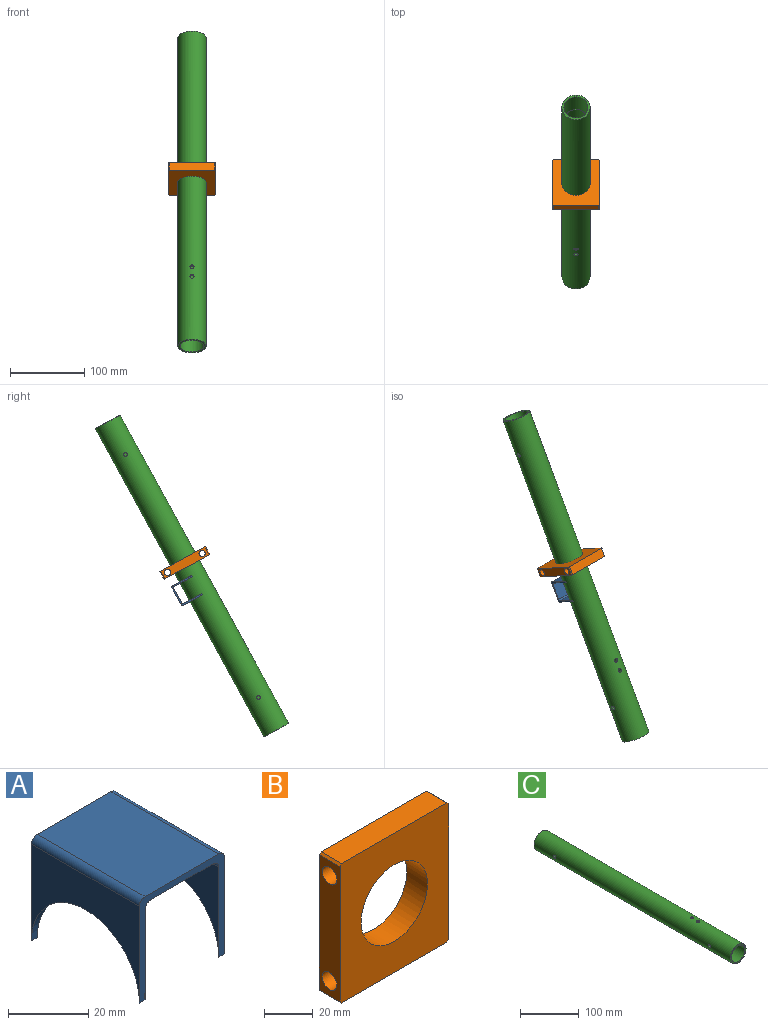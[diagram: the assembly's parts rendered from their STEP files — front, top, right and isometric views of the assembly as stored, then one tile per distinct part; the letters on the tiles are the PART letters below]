
ASSEMBLY  parts=3 mates=2
PART A: 14 faces, bbox 30x38x31.5 mm
  f0: plane 38x29.5mm, normal (1,0,0), area 553.9mm2, adj f6,f7,f9,f10
  f1: plane 38x26mm, normal (0,0,1), area 988mm2, adj f6,f7,f10,f11
  f2: plane 38x29.5mm, normal (-1,0,0), area 553.9mm2, adj f6,f7,f8,f11
  f3: plane 38x27.5mm, normal (1,0,0), area 477.9mm2, adj f6,f7,f8,f12
  f4: plane 38x22mm, normal (0,0,-1), area 836mm2, adj f6,f7,f12,f13
  f5: plane 38x27.5mm, normal (-1,0,0), area 477.9mm2, adj f6,f7,f9,f13
  f6: plane 31.5x30mm, normal (0,-1,0), area 178mm2, adj f0,f1,f2,f3,f4,f5,f8,f9
  f7: plane 31.5x30mm, normal (0,1,0), area 178mm2, adj f0,f1,f2,f3,f4,f5,f8,f9
  f8: cylinder r=19mm len=38mm, axis (-1,0,0), area 119.4mm2, adj f2,f3,f6,f7
  f9: cylinder r=19mm len=38mm, axis (-1,0,0), area 119.4mm2, adj f0,f5,f6,f7
  f10: cylinder r=2mm len=38mm, axis (0,1,0), area 119.4mm2, adj f0,f1,f6,f7
  f11: cylinder r=2mm len=38mm, axis (0,1,0), area 119.4mm2, adj f1,f2,f6,f7
  f12: cylinder r=2mm len=38mm, axis (0,-1,0), area 119.4mm2, adj f3,f4,f6,f7
  f13: cylinder r=2mm len=38mm, axis (0,-1,0), area 119.4mm2, adj f4,f5,f6,f7
PART B: 13 faces, bbox 63x12x70 mm
  f0: plane 61x12mm, normal (0,0,1), area 732mm2, adj f4,f5,f9,f12
  f1: plane 68x12mm, normal (-1,0,0), area 702.5mm2, adj f4,f5,f7,f8,f9,f10
  f2: plane 61x12mm, normal (0,0,-1), area 732mm2, adj f4,f5,f10,f11
  f3: plane 68x12mm, normal (1,0,0), area 702.5mm2, adj f4,f5,f7,f8,f11,f12
  f4: plane 70x63mm, normal (0,-1,0), area 3243.8mm2, adj f0,f1,f2,f3,f6,f9,f10,f11
  f5: plane 70x63mm, normal (0,1,0), area 3243.8mm2, adj f0,f1,f2,f3,f6,f9,f10,f11
  f6: cylinder r=19.25mm len=38.5mm, axis (0,-1,0), area 1451.4mm2, adj f4,f5
  f7: cylinder r=4.25mm len=63mm, axis (-1,0,0), area 1682.3mm2, adj f1,f3
  f8: cylinder r=4.25mm len=63mm, axis (-1,0,0), area 1682.3mm2, adj f1,f3
  f9: plane 12x1mm, normal (-0.71,0,0.71), area 17mm2, adj f0,f1,f4,f5
  f10: plane 12x1mm, normal (-0.71,0,-0.71), area 17mm2, adj f1,f2,f4,f5
  f11: plane 12x1mm, normal (0.71,0,-0.71), area 17mm2, adj f2,f3,f4,f5
  f12: plane 12x1mm, normal (0.71,0,0.71), area 17mm2, adj f0,f3,f4,f5
PART C: 12 faces, bbox 38x473x38 mm
  f0: cylinder r=16mm len=403mm, axis (0,-1,0), area 40426.7mm2, adj f4,f6,f8,f9,f10,f11
  f1: cylinder r=19mm len=473mm, axis (0,-1,0), area 56379.9mm2, adj f2,f3,f8,f9,f10,f11
  f2: plane 38x38mm, normal (0,1,0), area 312.2mm2, adj f1,f7
  f3: plane 38x38mm, normal (0,-1,0), area 312.2mm2, adj f1,f5
  f4: plane 32.35x32.35mm, normal (0,-1,0), area 17.7mm2, adj f0,f5
  f5: cylinder r=16.17mm len=35mm, axis (0,-1,0), area 3557.1mm2, adj f3,f4
  f6: plane 32.35x32.35mm, normal (0,1,0), area 17.7mm2, adj f0,f7
  f7: cylinder r=16.17mm len=35mm, axis (0,1,0), area 3557.1mm2, adj f2,f6
  f8: cylinder r=2.75mm len=5.5mm, axis (0,0,1), area 52.2mm2, adj f0,f1
  f9: cylinder r=2.75mm len=5.5mm, axis (0,0,1), area 52.2mm2, adj f0,f1
  f10: cylinder r=2.5mm len=5mm, axis (-1,0,0), area 47.4mm2, adj f0,f1
  f11: cylinder r=2.5mm len=5mm, axis (-1,0,0), area 47.4mm2, adj f0,f1
PLACE A rot(axis=(-0.65,-0.65,-0.39),137.7deg) t=(40.81,-78.19,244.19)mm
PLACE B rot(axis=(1,0,0),61.3deg) t=(-9.69,-22.04,273.89)mm
PLACE C rot(axis=(1,0,0),61.3deg) t=(21.81,-178.74,60.4)mm
MATE revolute A.f8 <-> C.f1  axis (0,-0.48,-0.88) through (21.81,-65.23,267.88)mm
MATE cylindrical B.f6 <-> C.f1  axis (0,-0.48,-0.88) through (21.81,-58.51,280.17)mm
